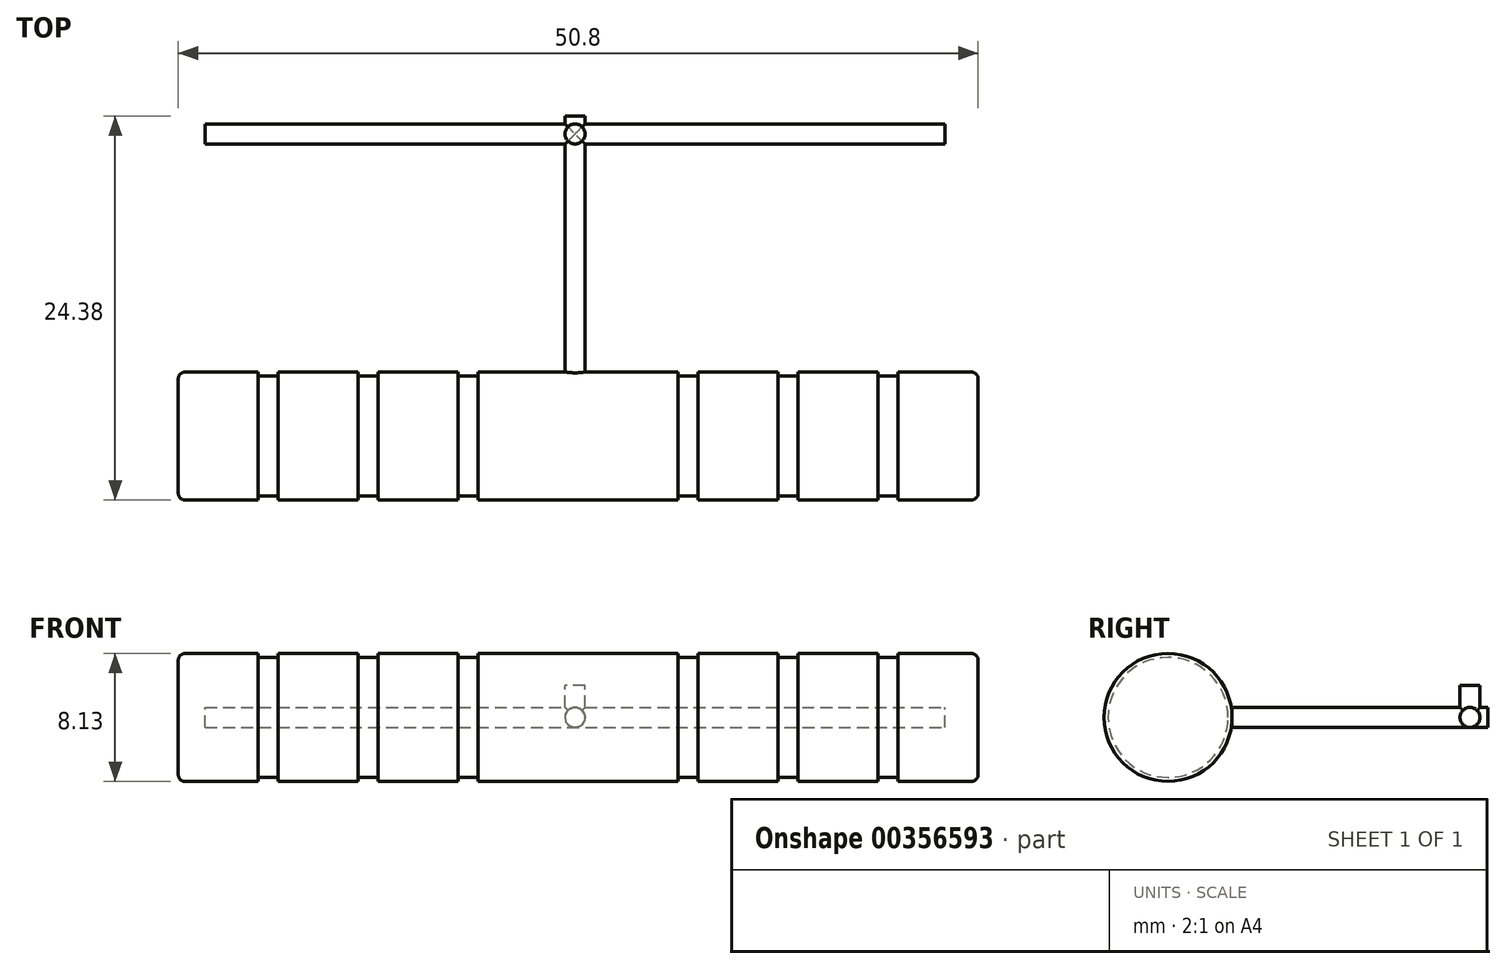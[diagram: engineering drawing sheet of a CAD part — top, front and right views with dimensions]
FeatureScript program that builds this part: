
annotation { "Feature Type Name" : "Feature", "Feature Type Description" : "" }
export const myFeature = defineFeature(function(context is Context, id is Id, definition is map)
    precondition{}
    {
        {
            var Q0;
            Q0=qCreatedBy(makeId("Front.planeOp"),FACE);
            var sketch = newSketch(context, id + "F0", { "sketchPlane" : qUnion([Q0])});
            skLineSegment(sketch, "E0", {"start": v(-402.85, -68.04) * mm, "end": v(-352.05, -68.04) * mm});
            skLineSegment(sketch, "E1", {"start": v(-377.45, -68.04) * mm, "end": v(-377.45, -67.78) * mm});
            skPoint(sketch, "E1.endSnap0", {"position": v(-377.45, -68.04) * mm});
            skLineSegment(sketch, "E2", {"start": v(-377.45, -67.78) * mm, "end": v(-371.1, -67.78) * mm});
            skLineSegment(sketch, "E3", {"start": v(-371.1, -67.78) * mm, "end": v(-371.1, -68.04) * mm});
            skLineSegment(sketch, "E4", {"start": v(-377.45, -67.78) * mm, "end": v(-383.8, -67.78) * mm});
            skLineSegment(sketch, "E5", {"start": v(-383.8, -67.78) * mm, "end": v(-383.8, -68.04) * mm});
            skLineSegment(sketch, "E6", {"start": v(-352.05, -68.04) * mm, "end": v(-352.05, -67.78) * mm});
            skLineSegment(sketch, "E7", {"start": v(-352.05, -67.78) * mm, "end": v(-357.13, -67.78) * mm});
            skLineSegment(sketch, "E8", {"start": v(-357.13, -67.78) * mm, "end": v(-357.13, -68.04) * mm});
            skLineSegment(sketch, "E9", {"start": v(-358.4, -68.04) * mm, "end": v(-358.4, -67.78) * mm});
            skLineSegment(sketch, "E10", {"start": v(-358.4, -67.78) * mm, "end": v(-363.48, -67.78) * mm});
            skLineSegment(sketch, "E11", {"start": v(-363.48, -67.78) * mm, "end": v(-363.48, -68.04) * mm});
            skLineSegment(sketch, "E12", {"start": v(-364.75, -68.04) * mm, "end": v(-364.75, -67.78) * mm});
            skLineSegment(sketch, "E13", {"start": v(-364.75, -67.78) * mm, "end": v(-369.83, -67.78) * mm});
            skLineSegment(sketch, "E14", {"start": v(-369.83, -67.78) * mm, "end": v(-369.83, -68.04) * mm});
            skLineSegment(sketch, "E15.MirrorCS", {"start": v(-402.85, -68.04) * mm, "end": v(-402.85, -67.78) * mm});
            skLineSegment(sketch, "E16.MirrorCS", {"start": v(-402.85, -67.78) * mm, "end": v(-397.77, -67.78) * mm});
            skLineSegment(sketch, "E17.MirrorCS", {"start": v(-397.77, -67.78) * mm, "end": v(-397.77, -68.04) * mm});
            skLineSegment(sketch, "E18.MirrorCS", {"start": v(-396.5, -68.04) * mm, "end": v(-396.5, -67.78) * mm});
            skLineSegment(sketch, "E19.MirrorCS", {"start": v(-396.5, -67.78) * mm, "end": v(-391.42, -67.78) * mm});
            skLineSegment(sketch, "E20.MirrorCS", {"start": v(-390.15, -68.04) * mm, "end": v(-390.15, -67.78) * mm});
            skLineSegment(sketch, "E21.MirrorCS", {"start": v(-390.15, -67.78) * mm, "end": v(-385.07, -67.78) * mm});
            skLineSegment(sketch, "E22.MirrorCS", {"start": v(-391.42, -67.78) * mm, "end": v(-391.42, -68.04) * mm});
            skLineSegment(sketch, "E23.MirrorCS", {"start": v(-385.07, -67.78) * mm, "end": v(-385.07, -68.04) * mm});
            skLineSegment(sketch, "E24", {"start": v(-352.05, -68.04) * mm, "end": v(-352.05, -71.85) * mm});
            skLineSegment(sketch, "E25", {"start": v(-352.05, -71.85) * mm, "end": v(-402.85, -71.85) * mm});
            skLineSegment(sketch, "E26", {"start": v(-402.85, -71.85) * mm, "end": v(-402.85, -68.04) * mm});
            skSolve(sketch);
        }
        {
            var Q0;
            Q0=qSketchRegion(id+"F0",true);
            var Q1;
            Q1=sQuery(id+"F0.wireOp",EDGE,"E25");
            revolve(context, id + "F1", {"entities" : qUnion([Q0]), "axis" : qUnion([Q1]), "revolveType" : RevolveType.FULL});
        }
        {
            var Q0;
            Q0=makeQuery(id+"F1.opRevolve","SWEPT_EDGE",EDGE,{"disambiguationData":[OSD([sQuery(id+"F0.wireOp",EDGE,"E6"),sQuery(id+"F0.wireOp",EDGE,"E7")])]});
            var Q1;
            Q1=makeQuery(id+"F1.opRevolve","SWEPT_EDGE",EDGE,{"disambiguationData":[OSD([sQuery(id+"F0.wireOp",EDGE,"E15.MirrorCS"),sQuery(id+"F0.wireOp",EDGE,"E16.MirrorCS")])]});
            fillet(context, id + "F2", {"entities" : qUnion([Q0, Q1]), "radius" : 0.43 * mm, "tangentPropagation" : true, "allowEdgeOverflow" : false});
        }
        {
            var Q0;
            Q0=qCreatedBy(makeId("Front.planeOp"),FACE);
            cPlane(context, id + "F3", {"entities" : qUnion([Q0]), "cplaneType" : CPlaneType.OFFSET, "offset" : 0 * mm, "width" : 152.4 * mm, "height" : 152.4 * mm});
        }
        {
            var Q0;
            Q0=qCreatedBy(id+"F3.planeOp",FACE);
            var sketch = newSketch(context, id + "F4", { "sketchPlane" : qUnion([Q0])});
            skCircle(sketch, "E27", {"center": v(-377.65, -71.85) * mm, "radius": 0.64 * mm});
            skSolve(sketch);
        }
        {
            var Q0;
            Q0=qSketchRegion(id+"F4",true);
            extrude(context, id + "F5", {"entities" : qUnion([Q0]), "operationType" : NewBodyOperationType.ADD, "oppositeDirection" : true, "depth" : 20.32 * mm});
        }
        {
            var Q0;
            Q0=qCreatedBy(makeId("Top.planeOp"),FACE);
            cPlane(context, id + "F6", {"entities" : qUnion([Q0]), "cplaneType" : CPlaneType.OFFSET, "offset" : 25.4 * mm, "width" : 152.4 * mm, "height" : 152.4 * mm});
        }
        {
            var Q0;
            Q0=qCreatedBy(id+"F6.planeOp",FACE);
            var sketch = newSketch(context, id + "F7", { "sketchPlane" : qUnion([Q0])});
            skCircle(sketch, "E28", {"center": v(-377.65, 19.19) * mm, "radius": 0.64 * mm});
            skSolve(sketch);
        }
        {
            var Q0;
            Q0=qSketchRegion(id+"F7",true);
            var Q1;
            Q1=sQuery(id+"F7.wireOp",EDGE,"E28");
            extrude(context, id + "F8", {"entities" : qUnion([Q0]), "operationType" : NewBodyOperationType.ADD, "surfaceEntities" : qUnion([Q1]), "oppositeDirection" : true, "depth" : 97.24 * mm, "hasSecondDirection" : true, "secondDirectionOppositeDirection" : true, "secondDirectionDepth" : 95.2 * mm});
        }
        {
            var Q0;
            Q0=qCreatedBy(makeId("Right.planeOp"),FACE);
            var sketch = newSketch(context, id + "F9", { "sketchPlane" : qUnion([Q0])});
            skLineSegment(sketch, "E29", {"start": v(21.22, -70.63) * mm, "end": v(21.22, -73.06) * mm});
            skLineSegment(sketch, "E30", {"start": v(21.22, -71.85) * mm, "end": v(19.18, -71.85) * mm});
            skPoint(sketch, "E30.endSnap0", {"position": v(21.22, -71.85) * mm});
            skCircle(sketch, "E31", {"center": v(19.18, -71.85) * mm, "radius": 0.64 * mm});
            skSolve(sketch);
        }
        {
            var Q0;
            Q0=makeQuery(id+"F9.imprint","IMPRINT",FACE,{"disambiguationData":[TD([[makeQuery(id+"F9.imprint","IMPRINT",EDGE,{"derivedFrom":sQuery(id+"F9.wireOp",EDGE,"E31")}),1.0]])]});
            extrude(context, id + "F10", {"entities" : qUnion([Q0]), "operationType" : NewBodyOperationType.ADD, "oppositeDirection" : true, "depth" : 401.14 * mm, "hasSecondDirection" : true, "secondDirectionOppositeDirection" : true, "secondDirectionDepth" : 354.15 * mm});
        }
    });
